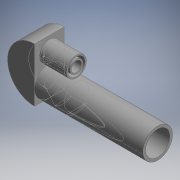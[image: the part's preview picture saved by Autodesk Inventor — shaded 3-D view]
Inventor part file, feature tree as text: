
AUTODESK INVENTOR PART (.ipt)
format: ipt  version: 2018 (Build 220112000, 112)  size: 236,544 bytes
history: native  units: in
note: dims shown in document units (in); Inventor stores cm internally (conversion verified against a paired STEP export)
features: other x7, extrude x5, sheet_metal_op x1, loft x1, fillet x1, projected_geometry x1, sketch x1
ambient origin geometry x8: Origin, YZ Plane, XZ Plane, XY Plane, X Axis, Y Axis, Z Axis, Center Point
bodies: Body1 (feature_tree)
feature tree (17):
  sheet_metal_op  "Bend"
  extrude  "Tube Socket"  Depth=0.3937in TaperAngle=0.0deg
  extrude  "Convert to Whistle"  Depth=0.1969in
  loft  "Path to Slit"
  extrude  "Whistle Adapter"  Depth=0.1969in TaperAngle=0.0deg
  extrude  "TubeSegment"  TaperAngle=0.0deg  [1 undecoded]
  extrude  "Edge Cut"  TaperAngle=0.0deg  [1 undecoded]
  fillet  "Fillet1"  Radius=0.1969in
  other  "BendSketch"
  other  "Tube Socket Sketch"
  other  "Convert to Whistle Sketch"
  other  "Slit Sketch"
  other  "Edges3"
  other  "Whistle Adapter Profile Sketch"
  projected_geometry  "Projected Loop3"
  sketch  "Sketch17"  dims[d38=0.4331in d65=0.3937in d66=0.0in d68=0.1969in d70=0.1875in d72=0.1969in d73=0.0in d76=0.0in d77=90.0deg d78=0.0in d79=90.0deg d80=0.1969in d81=0.0in d82=0.1969in d83=0.0394in d86=1.1811in d87=0.0in d89=1.1811in d90=0.0in d91=0.0079in d92=0.3543in d93=0.0344in]
  other  "Edge Cut Sketch"
note: 2 required parameter values undecoded (feature->parameter linkage not recoverable at this tier; creation-order binding heuristic only, values carry confidence <= 0.55)
